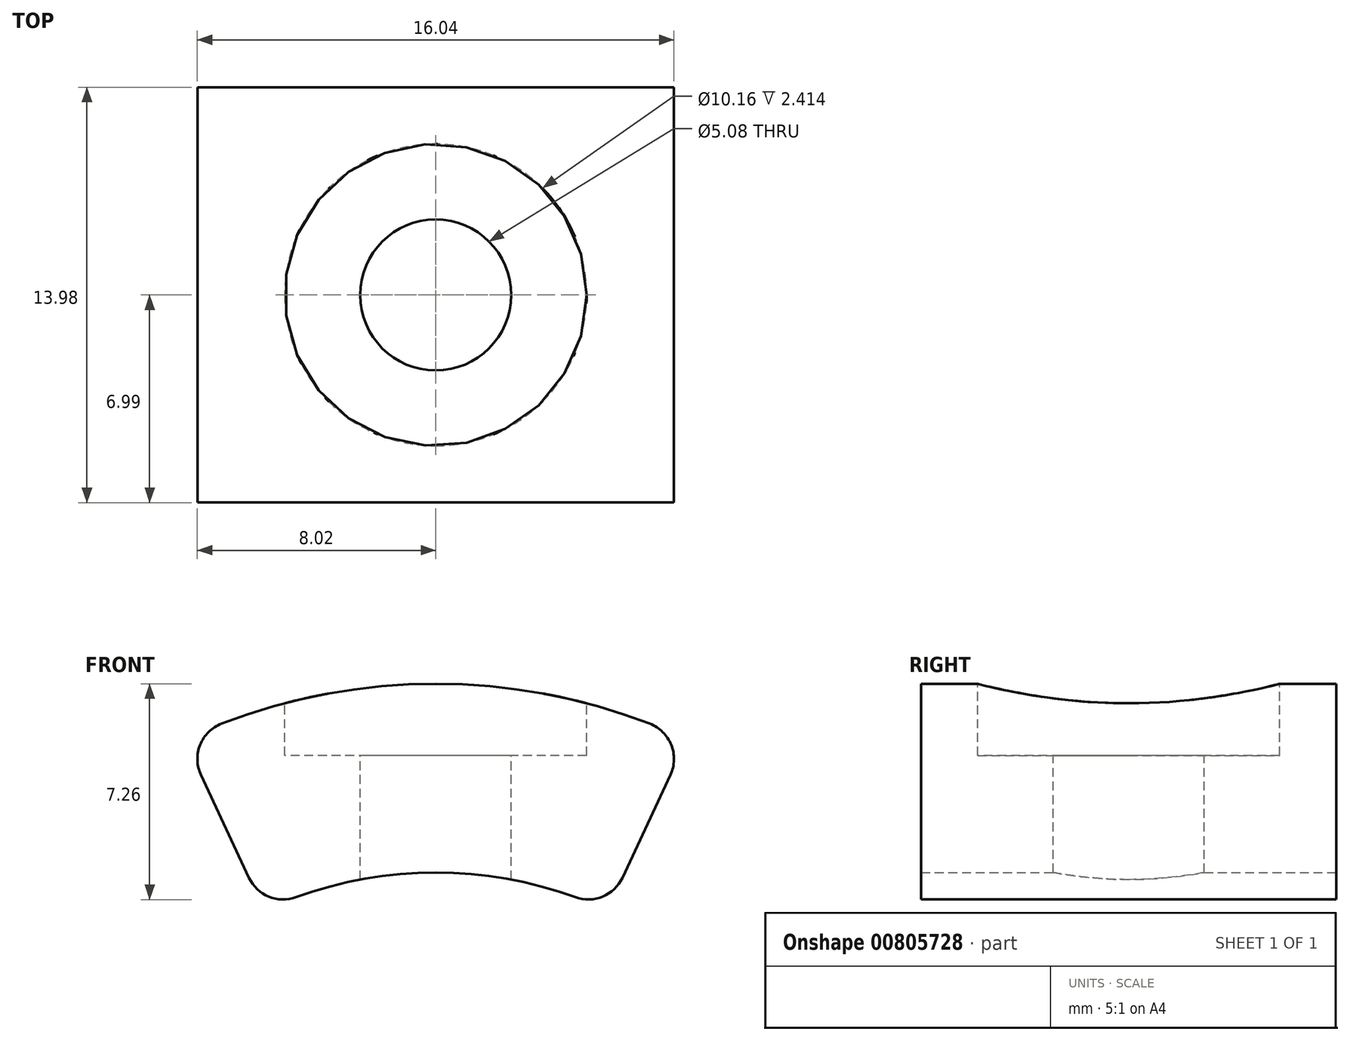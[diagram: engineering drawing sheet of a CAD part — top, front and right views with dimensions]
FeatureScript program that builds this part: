
annotation { "Feature Type Name" : "Feature", "Feature Type Description" : "" }
export const myFeature = defineFeature(function(context is Context, id is Id, definition is map)
    precondition{}
    {
        {
            var Q0;
            Q0=qCreatedBy(makeId("Front.planeOp"),FACE);
            var sketch = newSketch(context, id + "F0", { "sketchPlane" : qUnion([Q0])});
            skCircle(sketch, "E0", {"center": v(0, 0) * mm, "radius": 13.65 * mm});
            skCircle(sketch, "E1.0", {"center": v(0, 0) * mm, "radius": 20 * mm});
            skLineSegment(sketch, "E2", {"start": v(0, 0) * mm, "end": v(-10.89, 23.35) * mm});
            skLineSegment(sketch, "E3", {"start": v(0, 0) * mm, "end": v(10.45, 22.4) * mm});
            skLineSegment(sketch, "E4", {"start": v(0, 0) * mm, "end": v(0, 29.5) * mm, "construction": true});
            skSolve(sketch);
        }
        {
            var Q0;
            {var subQ0=sQuery(id+"F0.wireOp",EDGE,"E2");var subQ1=sQuery(id+"F0.wireOp",EDGE,"E0");var subQ2=makeQuery(id+"F0.imprint","INTERSECT",VERTEX,{"derivedFrom":[subQ1,subQ0]});Q0=makeQuery(id+"F0.imprint","IMPRINT",FACE,{"disambiguationData":[TD([[makeQuery(id+"F0.imprint","IMPRINT",EDGE,{"disambiguationData":[TD([[subQ2,1.0]])],"derivedFrom":subQ1}),-1.0]])]});}
            extrude(context, id + "F1", {"entities" : qUnion([Q0]), "depth" : 13.97 * mm, "offsetDistance" : 25.4 * mm, "symmetric" : true});
        }
        {
            var Q0;
            Q0=makeQuery(id+"F1.opExtrude","CAP_EDGE",EDGE,{"disambiguationData":[OSD([sQuery(id+"F0.wireOp",EDGE,"E1.0")])],"isStart":false});
            cPoint(context, id + "F2", {"entities" : qUnion([Q0]), "parameter" : 0.5});
        }
        {
            var Q0;
            Q0=qCreatedBy(makeId("Top.planeOp"),FACE);
            var Q1;
            Q1 = qCreatedBy(id + "F2" ,VERTEX);
            cPlane(context, id + "F3", {"entities" : qUnion([Q0, Q1]), "cplaneType" : CPlaneType.PLANE_POINT, "offset" : 25.4 * mm, "width" : 152.4 * mm, "height" : 152.4 * mm});
        }
        {
            var Q0;
            Q0=qCreatedBy(id+"F3.planeOp",FACE);
            var sketch = newSketch(context, id + "F4", { "sketchPlane" : qUnion([Q0])});
            skCircle(sketch, "E5", {"center": v(0, 0) * mm, "radius": 5.08 * mm});
            skSolve(sketch);
        }
        {
            var Q0;
            Q0=makeQuery(id+"F4.imprint","IMPRINT",FACE,{"disambiguationData":[TD([[makeQuery(id+"F4.imprint","IMPRINT",EDGE,{"derivedFrom":sQuery(id+"F4.wireOp",EDGE,"E5")}),1.0]])]});
            extrude(context, id + "F5", {"entities" : qUnion([Q0]), "operationType" : NewBodyOperationType.REMOVE, "oppositeDirection" : true, "depth" : 2.41 * mm, "offsetDistance" : 25.4 * mm});
        }
        {
            var Q0;
            Q0=makeQuery(id+"F5.boolean.opBoolean","COPY",FACE,{"derivedFrom":makeQuery(id+"F5.opExtrude","CAP_FACE",FACE,{"disambiguationData":[OSD([sQuery(id+"F4.wireOp",EDGE,"E5")])],"isStart":false})});
            var sketch = newSketch(context, id + "F6", { "sketchPlane" : qUnion([Q0])});
            skCircle(sketch, "E6", {"center": v(0, 0) * mm, "radius": 2.54 * mm});
            skSolve(sketch);
        }
        {
            var Q0;
            Q0 = qSketchRegion(id + "F6", true);
            extrude(context, id + "F7", {"entities" : qUnion([Q0]), "operationType" : NewBodyOperationType.REMOVE, "endBound" : BoundingType.THROUGH_ALL, "oppositeDirection" : true, "depth" : 25.4 * mm, "offsetDistance" : 25.4 * mm});
        }
        {
            var Q0;
            Q0=makeQuery(id+"F1.opExtrude","SWEPT_EDGE",EDGE,{"disambiguationData":[OSD([sQuery(id+"F0.wireOp",EDGE,"E1.0"),sQuery(id+"F0.wireOp",EDGE,"E3")])]});
            var Q1;
            Q1=makeQuery(id+"F1.opExtrude","SWEPT_EDGE",EDGE,{"disambiguationData":[OSD([sQuery(id+"F0.wireOp",EDGE,"E1.0"),sQuery(id+"F0.wireOp",EDGE,"E2")])]});
            var Q2;
            Q2=makeQuery(id+"F1.opExtrude","SWEPT_EDGE",EDGE,{"disambiguationData":[OSD([sQuery(id+"F0.wireOp",EDGE,"E0"),sQuery(id+"F0.wireOp",EDGE,"E3")])]});
            var Q3;
            Q3=makeQuery(id+"F1.opExtrude","SWEPT_EDGE",EDGE,{"disambiguationData":[OSD([sQuery(id+"F0.wireOp",EDGE,"E0"),sQuery(id+"F0.wireOp",EDGE,"E2")])]});
            fillet(context, id + "F8", {"entities" : qUnion([Q0, Q1, Q2, Q3]), "radius" : 1.27 * mm, "tangentPropagation" : true, "allowEdgeOverflow" : false});
        }
    });
